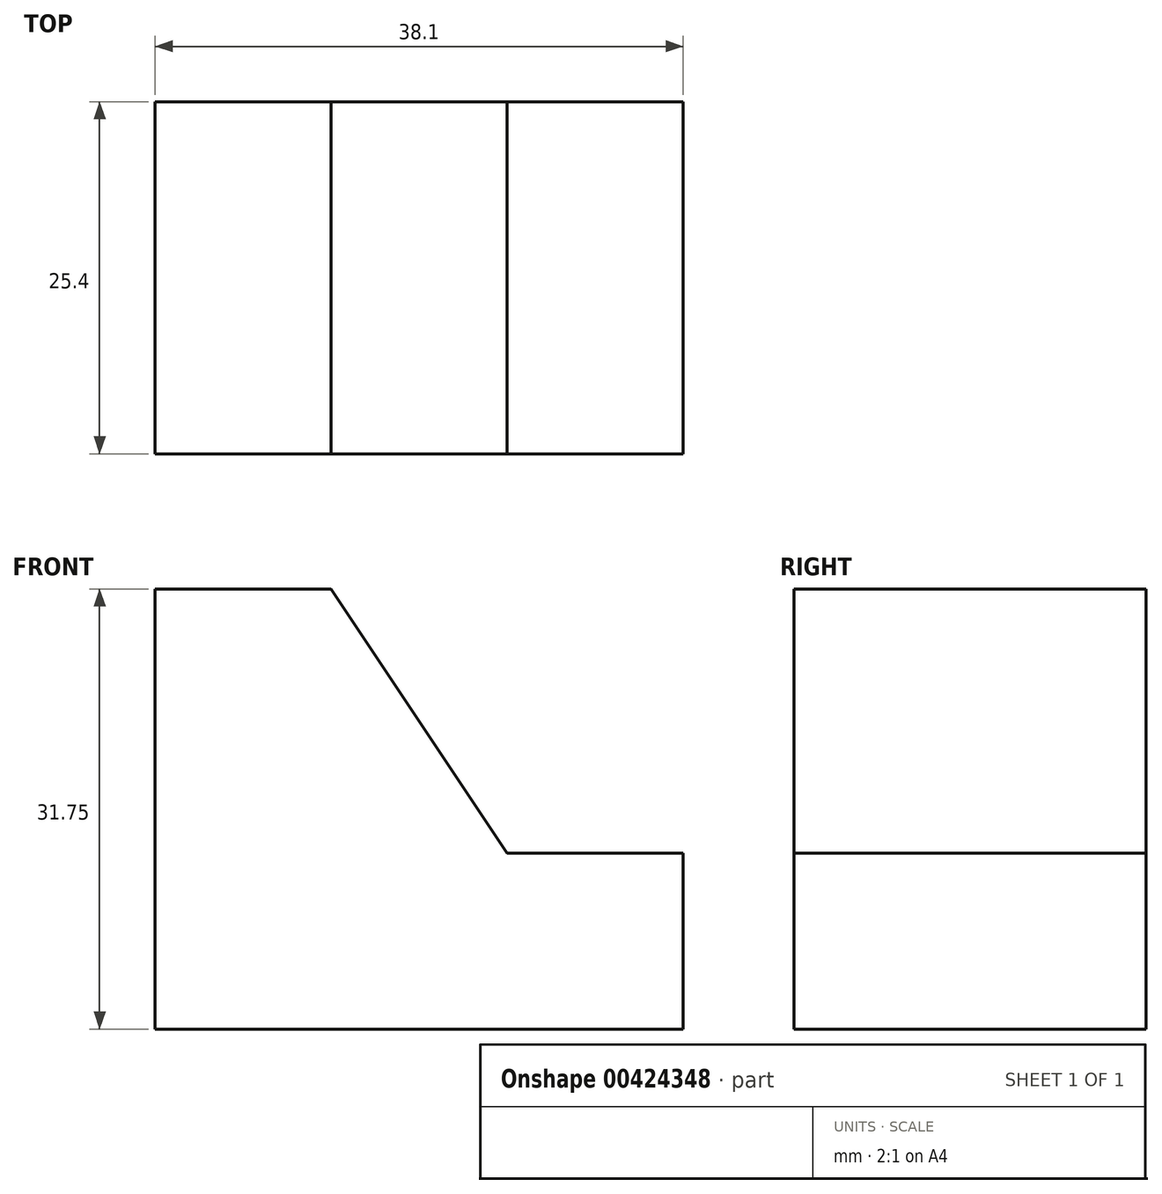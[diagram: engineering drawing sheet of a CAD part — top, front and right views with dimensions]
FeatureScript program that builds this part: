
annotation { "Feature Type Name" : "Feature", "Feature Type Description" : "" }
export const myFeature = defineFeature(function(context is Context, id is Id, definition is map)
    precondition{}
    {
        {
            var Q0;
            Q0=qCreatedBy(makeId("Front.planeOp"),FACE);
            var sketch = newSketch(context, id + "F0", { "sketchPlane" : qUnion([Q0])});
            skLineSegment(sketch, "E0", {"start": v(0, 0) * mm, "end": v(0, 31.75) * mm});
            skLineSegment(sketch, "E1", {"start": v(0, 31.75) * mm, "end": v(12.7, 31.75) * mm});
            skLineSegment(sketch, "E2", {"start": v(0, 0) * mm, "end": v(38.1, 0) * mm});
            skLineSegment(sketch, "E3", {"start": v(38.1, 0) * mm, "end": v(38.1, 12.7) * mm});
            skLineSegment(sketch, "E4", {"start": v(38.1, 12.7) * mm, "end": v(25.4, 12.7) * mm});
            skLineSegment(sketch, "E5", {"start": v(12.7, 31.75) * mm, "end": v(25.4, 12.7) * mm});
            skSolve(sketch);
        }
        {
            var Q0;
            Q0=makeQuery(id+"F0.imprint","IMPRINT",FACE,{"disambiguationData":[TD([[makeQuery(id+"F0.imprint","IMPRINT",EDGE,{"derivedFrom":sQuery(id+"F0.wireOp",EDGE,"E0")}),-1.0]])]});
            extrude(context, id + "F1", {"entities" : qUnion([Q0]), "depth" : 25.4 * mm});
        }
    });
